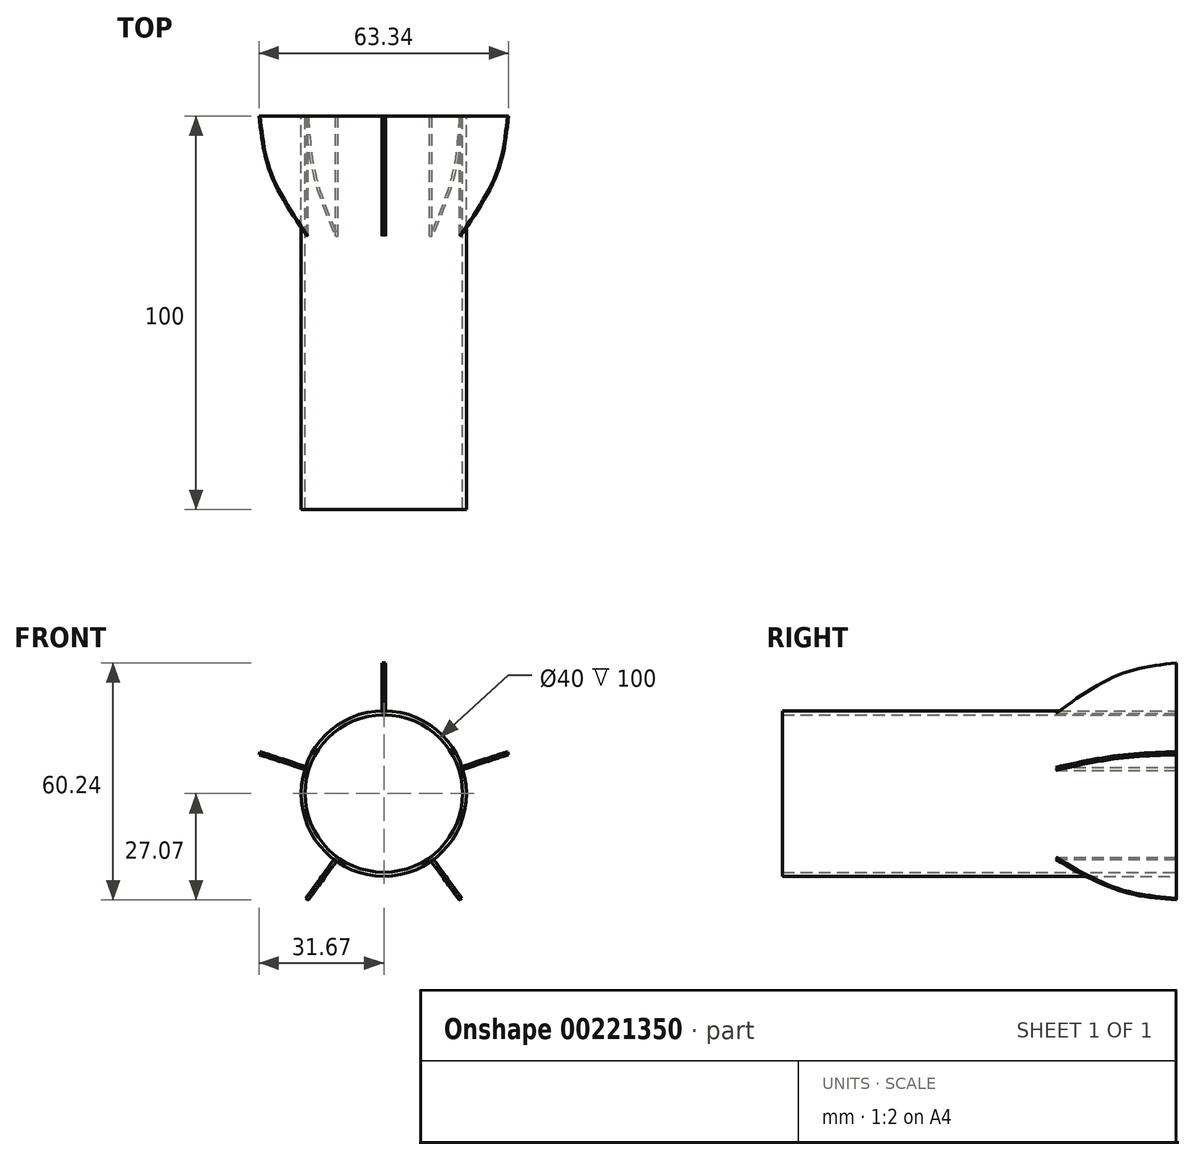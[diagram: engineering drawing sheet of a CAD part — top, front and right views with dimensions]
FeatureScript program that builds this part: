
annotation { "Feature Type Name" : "Feature", "Feature Type Description" : "" }
export const myFeature = defineFeature(function(context is Context, id is Id, definition is map)
    precondition{}
    {
        {
            var Q0;
            Q0=qCreatedBy(makeId("Front.planeOp"),FACE);
            var sketch = newSketch(context, id + "F0", { "sketchPlane" : qUnion([Q0])});
            skCircle(sketch, "E0", {"center": v(0, 0) * mm, "radius": 20 * mm});
            skCircle(sketch, "E1", {"center": v(0, 0) * mm, "radius": 21 * mm});
            skSolve(sketch);
        }
        {
            var Q0;
            Q0=makeQuery(id+"F0.imprint","IMPRINT",FACE,{"disambiguationData":[TD([[makeQuery(id+"F0.imprint","IMPRINT",EDGE,{"derivedFrom":sQuery(id+"F0.wireOp",EDGE,"E0")}),-1.0]])]});
            extrude(context, id + "F1", {"entities" : qUnion([Q0]), "depth" : 100 * mm});
        }
        {
            var Q0;
            Q0=qCreatedBy(makeId("Right.planeOp"),FACE);
            var sketch = newSketch(context, id + "F2", { "sketchPlane" : qUnion([Q0])});
            skLineSegment(sketch, "E2", {"start": v(-30.6, 20.35) * mm, "end": v(0, 20.35) * mm});
            skLineSegment(sketch, "E3", {"start": v(0, 20.35) * mm, "end": v(0, 33.17) * mm});
            skFitSpline(sketch, "E4", {"points": [v(0, 33.17) * mm, v(-14.35, 30.26) * mm, v(-30.6, 20.35) * mm], "startDerivative": vector(-30.77, -3.32) * mm, "endDerivative": vector(-30.42, -21.91) * mm});
            skSolve(sketch);
        }
        {
            var Q0;
            Q0 = qSketchRegion(id + "F2", true);
            extrude(context, id + "F3", {"entities" : qUnion([Q0]), "endBound" : BoundingType.SYMMETRIC, "depth" : 0.8 * mm});
        }
        {
            var Q0;
            Q0=makeQuery(id+"F3.opExtrude","SWEPT_BODY",BODY,{"disambiguationData":[OSD([sQuery(id+"F2.wireOp",EDGE,"E2"),sQuery(id+"F2.wireOp",EDGE,"E3"),sQuery(id+"F2.wireOp",EDGE,"E4")])]});
            var Q1;
            Q1=makeQuery(id+"F1.opExtrude","SWEPT_FACE",FACE,{"disambiguationData":[OSD([sQuery(id+"F0.wireOp",EDGE,"E1")])]});
            circularPattern(context, id + "F4", {"entities" : qUnion([Q0]), "axis" : qUnion([Q1]), "angle" : 360 * degree, "instanceCount" : 5, "equalSpace" : true});
        }
    });
